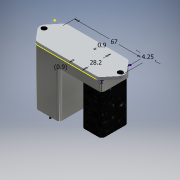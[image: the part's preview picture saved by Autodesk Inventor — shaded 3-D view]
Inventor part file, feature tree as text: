
AUTODESK INVENTOR PART (.ipt)
format: ipt  version: 2018 (Build 220112000, 112)  size: 238,080 bytes
history: native  units: mm
features: sketch x6, extrude x5, hole x1
ambient origin geometry x8: Origin, YZ Plane, XZ Plane, XY Plane, X Axis, Y Axis, Z Axis, Center Point
bodies: Volumenkörper1 (feature_tree)
feature tree (12):
  extrude  "Extrusion1"  Depth=12.0mm
  hole  "Bohrung1"  [1 undecoded]
  extrude  "Extrusion2"  Depth=2.0mm
  extrude  "Extrusion3"  Depth=67.0mm
  extrude  "Extrusion4"  Depth=3.1mm
  extrude  "Extrusion5"  Depth=25.0mm
  sketch  "Skizze1"  dims[d2=12.0mm d3=12.0mm]
  sketch  "Skizze2"  dims[d6=4.5mm d7=2.8mm d8=0.0mm]
  sketch  "Skizze3"  dims[d9=75.5mm d10=2.0mm]
  sketch  "Skizze4"  dims[d11=3.2mm d12=6.0mm d13=5.0mm d14=2.0mm d15=90.0deg d16=8.0mm d17=20.594885mm d20=67.0mm]
  sketch  "Skizze5"  dims[d21=4.25mm d22=3.1mm]
  sketch  "Skizze6"  dims[d23=10.0mm d24=0.0mm d25=25.0mm d26=3.1mm d27=0.0mm d28=3.1mm d29=46.0mm d30=0.0mm d31=0.4mm d33=0.8mm d35=4.8mm d37=11.6mm d38=8.0mm d39=0.0mm d40=20.0mm d41=3.1mm d42=40.2mm d43=0.0mm d44=28.2mm d45=0.9mm d46=0.9mm d47=71.5mm d48=21.0mm d49=21.0mm d50=58.0mm d51=58.0mm d52=15.0mm d53=15.0mm d54=8.791223mm d55=8.791223mm d56=8.788764mm d57=8.788764mm d58=0.9mm d59=0.9mm d60=0.9mm d61=26.4mm d62=0.8mm d63=0.8mm d64=4.8mm d65=4.8mm d66=6.0mm d67=6.0mm d68=0.0mm d69=9.0mm]
note: 1 required parameter value undecoded (feature->parameter linkage not recoverable at this tier; creation-order binding heuristic only, values carry confidence <= 0.55)
